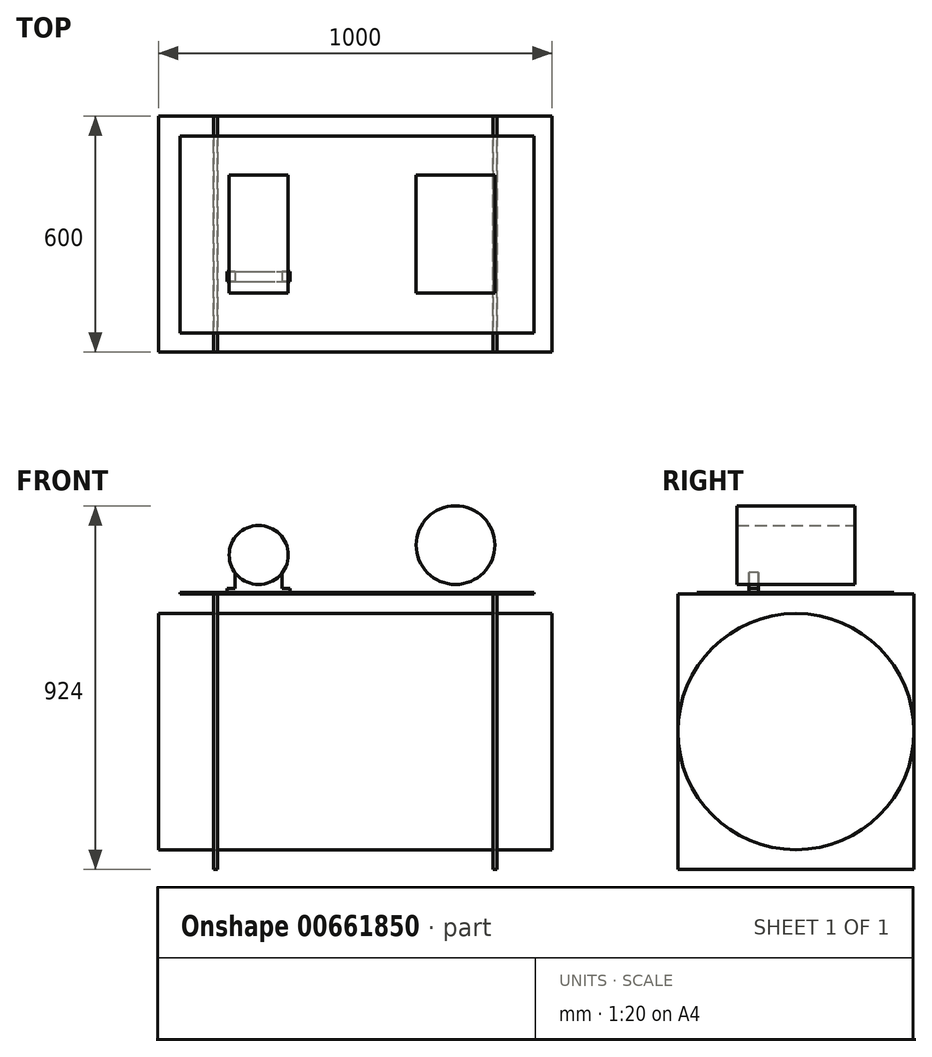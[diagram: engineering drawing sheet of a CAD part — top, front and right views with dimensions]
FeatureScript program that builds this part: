
annotation { "Feature Type Name" : "Feature", "Feature Type Description" : "" }
export const myFeature = defineFeature(function(context is Context, id is Id, definition is map)
    precondition{}
    {
        {
            var Q0;
            Q0=qCreatedBy(makeId("Right.planeOp"),FACE);
            var sketch = newSketch(context, id + "F0", { "sketchPlane" : qUnion([Q0])});
            skCircle(sketch, "E0", {"center": v(0, 0) * mm, "radius": 300 * mm});
            skSolve(sketch);
        }
        {
            var Q0;
            Q0 = qSketchRegion(id + "F0", true);
            extrude(context, id + "F1", {"entities" : qUnion([Q0]), "oppositeDirection" : true, "depth" : 1000 * mm, "offsetDistance" : 25 * mm});
        }
        {
            var Q0;
            Q0=qCreatedBy(makeId("Right.planeOp"),FACE);
            cPlane(context, id + "F2", {"entities" : qUnion([Q0]), "cplaneType" : CPlaneType.OFFSET, "offset" : 150 * mm, "oppositeDirection" : true, "width" : 150 * mm, "height" : 150 * mm});
        }
        {
            var Q0;
            Q0=qCreatedBy(id+"F2.planeOp",FACE);
            var sketch = newSketch(context, id + "F3", { "sketchPlane" : qUnion([Q0])});
            skCircle(sketch, "E1.0", {"center": v(0, 0) * mm, "radius": 300 * mm});
            skLineSegment(sketch, "E2", {"start": v(-300, 0) * mm, "end": v(-300, -350) * mm});
            skLineSegment(sketch, "E3", {"start": v(-300, -350) * mm, "end": v(300, -350) * mm});
            skLineSegment(sketch, "E4", {"start": v(300, -350) * mm, "end": v(300, 0) * mm});
            skSolve(sketch);
        }
        {
            var Q0;
            Q0 = qSketchRegion(id + "F3", true);
            extrude(context, id + "F4", {"entities" : qUnion([Q0]), "depth" : 10 * mm, "offsetDistance" : 25 * mm});
        }
        {
            var Q0;
            Q0=qCreatedBy(makeId("Right.planeOp"),FACE);
            cPlane(context, id + "F5", {"entities" : qUnion([Q0]), "cplaneType" : CPlaneType.OFFSET, "offset" : 500 * mm, "oppositeDirection" : true, "width" : 150 * mm, "height" : 150 * mm});
        }
        {
            var Q0;
            Q0=makeQuery(id+"F4.opExtrude","SWEPT_BODY",BODY,{"disambiguationData":[OSD([sQuery(id+"F3.wireOp",EDGE,"E1.0"),sQuery(id+"F3.wireOp",EDGE,"E2"),sQuery(id+"F3.wireOp",EDGE,"E3"),sQuery(id+"F3.wireOp",EDGE,"E4")])]});
            var Q1;
            Q1=qCreatedBy(id+"F5.planeOp",FACE);
            mirror(context, id + "F6", {"entities" : qUnion([Q0]), "mirrorPlane" : qUnion([Q1])});
        }
        {
            var Q0;
            Q0=makeQuery(id+"F4.opExtrude","SWEPT_BODY",BODY,{"disambiguationData":[OSD([sQuery(id+"F3.wireOp",EDGE,"E1.0"),sQuery(id+"F3.wireOp",EDGE,"E2"),sQuery(id+"F3.wireOp",EDGE,"E3"),sQuery(id+"F3.wireOp",EDGE,"E4")])]});
            var Q1;
            Q1=makeQuery(id+"F6.opPattern","COPY",BODY,{"derivedFrom":makeQuery(id+"F4.opExtrude","SWEPT_BODY",BODY,{"disambiguationData":[OSD([sQuery(id+"F3.wireOp",EDGE,"E1.0"),sQuery(id+"F3.wireOp",EDGE,"E2"),sQuery(id+"F3.wireOp",EDGE,"E3"),sQuery(id+"F3.wireOp",EDGE,"E4")])]}),"instanceName":"1"});
            var Q2;
            Q2=qCreatedBy(makeId("Top.planeOp"),FACE);
            mirror(context, id + "F7", {"entities" : qUnion([Q0, Q1]), "mirrorPlane" : qUnion([Q2])});
        }
        {
            var Q0;
            Q0=makeQuery(id+"F7.opPattern","COPY",FACE,{"derivedFrom":makeQuery(id+"F6.opPattern","COPY",FACE,{"derivedFrom":makeQuery(id+"F4.opExtrude","SWEPT_FACE",FACE,{"disambiguationData":[OSD([sQuery(id+"F3.wireOp",EDGE,"E3")])]}),"instanceName":"1"}),"instanceName":"1"});
            var sketch = newSketch(context, id + "F8", { "sketchPlane" : qUnion([Q0])});
            skLineSegment(sketch, "E5.bottom", {"start": v(-945, 249) * mm, "end": v(-45, 249) * mm});
            skLineSegment(sketch, "E5.top", {"start": v(-945, -251) * mm, "end": v(-45, -251) * mm});
            skLineSegment(sketch, "E5.left", {"start": v(-945, 249) * mm, "end": v(-945, -251) * mm});
            skLineSegment(sketch, "E5.right", {"start": v(-45, 249) * mm, "end": v(-45, -251) * mm});
            skLineSegment(sketch, "E6.0", {"start": v(-860, 300) * mm, "end": v(-850, 300) * mm});
            skLineSegment(sketch, "E7.0", {"start": v(-1000, 300) * mm, "end": v(-1000, -300) * mm});
            skSolve(sketch);
        }
        {
            var Q0;
            {var subQ0=sQuery(id+"F8.wireOp",EDGE,"E5.left");Q0=makeQuery(id+"F8.imprint","IMPRINT",FACE,{"disambiguationData":[TD([[makeQuery(id+"F8.imprint","IMPRINT",EDGE,{"derivedFrom":subQ0}),1.0]])]});}
            var Q1;
            {var subQ0=sQuery(id+"F8.wireOp",EDGE,"E5.right");Q1=makeQuery(id+"F8.imprint","IMPRINT",FACE,{"disambiguationData":[TD([[makeQuery(id+"F8.imprint","IMPRINT",EDGE,{"derivedFrom":subQ0}),-1.0]])]});}
            var Q2;
            {var subQ0=sQuery(id+"F8.wireOp",EDGE,"E5.bottom");var subQ1=sQuery(id+"F3.wireOp",EDGE,"E3");var subQ2=makeQuery(id+"F7.opPattern","COPY",EDGE,{"derivedFrom":makeQuery(id+"F6.opPattern","COPY",EDGE,{"derivedFrom":makeQuery(id+"F4.opExtrude","CAP_EDGE",EDGE,{"disambiguationData":[OSD([subQ1])],"isStart":false}),"instanceName":"1"}),"instanceName":"1"});var subQ3=makeQuery(id+"F8.imprint","INTERSECT",VERTEX,{"derivedFrom":[subQ2,subQ0]});Q2=makeQuery(id+"F8.imprint","IMPRINT",FACE,{"disambiguationData":[TD([[makeQuery(id+"F8.imprint","IMPRINT",EDGE,{"disambiguationData":[TD([[subQ3,-1.0]])],"derivedFrom":subQ0}),-1.0]])]});}
            extrude(context, id + "F9", {"entities" : qUnion([Q0, Q1, Q2]), "depth" : 4 * mm, "offsetDistance" : 25 * mm});
        }
        {
            var Q0;
            Q0=qCreatedBy(makeId("Front.planeOp"),FACE);
            var sketch = newSketch(context, id + "F10", { "sketchPlane" : qUnion([Q0])});
            skCircle(sketch, "E8", {"center": v(-745, 449) * mm, "radius": 75 * mm});
            skCircle(sketch, "E9", {"center": v(-245, 474) * mm, "radius": 100 * mm});
            skSolve(sketch);
        }
        {
            var Q0;
            Q0=makeQuery(id+"F10.imprint","IMPRINT",FACE,{"disambiguationData":[TD([[makeQuery(id+"F10.imprint","IMPRINT",EDGE,{"derivedFrom":sQuery(id+"F10.wireOp",EDGE,"E8")}),1.0]])]});
            var Q1;
            Q1=makeQuery(id+"F10.imprint","IMPRINT",FACE,{"disambiguationData":[TD([[makeQuery(id+"F10.imprint","IMPRINT",EDGE,{"derivedFrom":sQuery(id+"F10.wireOp",EDGE,"E9")}),1.0]])]});
            extrude(context, id + "F11", {"entities" : qUnion([Q0, Q1]), "endBound" : BoundingType.SYMMETRIC, "depth" : 300 * mm, "offsetDistance" : 25 * mm});
        }
        {
            var Q0;
            Q0=qCreatedBy(makeId("Front.planeOp"),FACE);
            cPlane(context, id + "F12", {"entities" : qUnion([Q0]), "cplaneType" : CPlaneType.OFFSET, "offset" : 120 * mm, "width" : 150 * mm, "height" : 150 * mm});
        }
        {
            var Q0;
            Q0=qCreatedBy(id+"F12.planeOp",FACE);
            var sketch = newSketch(context, id + "F13", { "sketchPlane" : qUnion([Q0])});
            skCircle(sketch, "E10.0", {"center": v(-745, 449) * mm, "radius": 75 * mm});
            skCircle(sketch, "E11.0", {"center": v(-245, 474) * mm, "radius": 100 * mm});
            skLineSegment(sketch, "E12", {"start": v(-805, 404) * mm, "end": v(-805, 364) * mm});
            skLineSegment(sketch, "E13", {"start": v(-805, 364) * mm, "end": v(-825, 364) * mm});
            skLineSegment(sketch, "E14.0", {"start": v(-945, 354) * mm, "end": v(-45, 354) * mm});
            skLineSegment(sketch, "E15", {"start": v(-825, 364) * mm, "end": v(-825, 354) * mm});
            skLineSegment(sketch, "E16", {"start": v(-825, 354) * mm, "end": v(-665, 354) * mm});
            skLineSegment(sketch, "E17", {"start": v(-665, 354) * mm, "end": v(-665, 364) * mm});
            skLineSegment(sketch, "E18", {"start": v(-665, 364) * mm, "end": v(-685, 364) * mm});
            skLineSegment(sketch, "E19", {"start": v(-685, 364) * mm, "end": v(-685, 404) * mm});
            skLineSegment(sketch, "E20", {"start": v(-745, 449) * mm, "end": v(-745, 416.55) * mm, "construction": true});
            skLineSegment(sketch, "E21", {"start": v(-335, 430.41) * mm, "end": v(-335, 364) * mm});
            skLineSegment(sketch, "E22", {"start": v(-335, 364) * mm, "end": v(-355, 364) * mm});
            skLineSegment(sketch, "E23", {"start": v(-355, 364) * mm, "end": v(-355, 354) * mm});
            skLineSegment(sketch, "E24", {"start": v(-355, 354) * mm, "end": v(-135, 354) * mm});
            skLineSegment(sketch, "E25", {"start": v(-135, 354) * mm, "end": v(-135, 364) * mm});
            skLineSegment(sketch, "E26", {"start": v(-135, 364) * mm, "end": v(-155, 364) * mm});
            skLineSegment(sketch, "E27", {"start": v(-155, 364) * mm, "end": v(-155, 430.41) * mm});
            skLineSegment(sketch, "E28", {"start": v(-245, 474) * mm, "end": v(-245, 436.46) * mm, "construction": true});
            skSolve(sketch);
        }
        {
            var Q0;
            {var subQ0=sQuery(id+"F13.wireOp",EDGE,"E12");Q0=makeQuery(id+"F13.imprint","IMPRINT",FACE,{"disambiguationData":[TD([[makeQuery(id+"F13.imprint","IMPRINT",EDGE,{"derivedFrom":subQ0}),1.0]])]});}
            var Q1;
            {var subQ0=sQuery(id+"F13.wireOp",EDGE,"E21");Q1=makeQuery(id+"F13.imprint","IMPRINT",FACE,{"disambiguationData":[TD([[makeQuery(id+"F13.imprint","IMPRINT",EDGE,{"derivedFrom":subQ0}),1.0]])]});}
            extrude(context, id + "F14", {"entities" : qUnion([Q0, Q1]), "operationType" : NewBodyOperationType.ADD, "oppositeDirection" : true, "depth" : 25 * mm, "offsetDistance" : 25 * mm});
        }
        {
            var Q0;
            Q0=makeQuery(id+"F11.opExtrude","SWEPT_BODY",BODY,{"disambiguationData":[OSD([sQuery(id+"F10.wireOp",EDGE,"E9")])]});
            var Q1;
            Q1=makeQuery(id+"F11.opExtrude","SWEPT_BODY",BODY,{"disambiguationData":[OSD([sQuery(id+"F10.wireOp",EDGE,"E8")])]});
            var Q2;
            Q2=qCreatedBy(makeId("Front.planeOp"),FACE);
            mirror(context, id + "F15", {"entities" : qUnion([Q0, Q1]), "mirrorPlane" : qUnion([Q2])});
        }
    });
